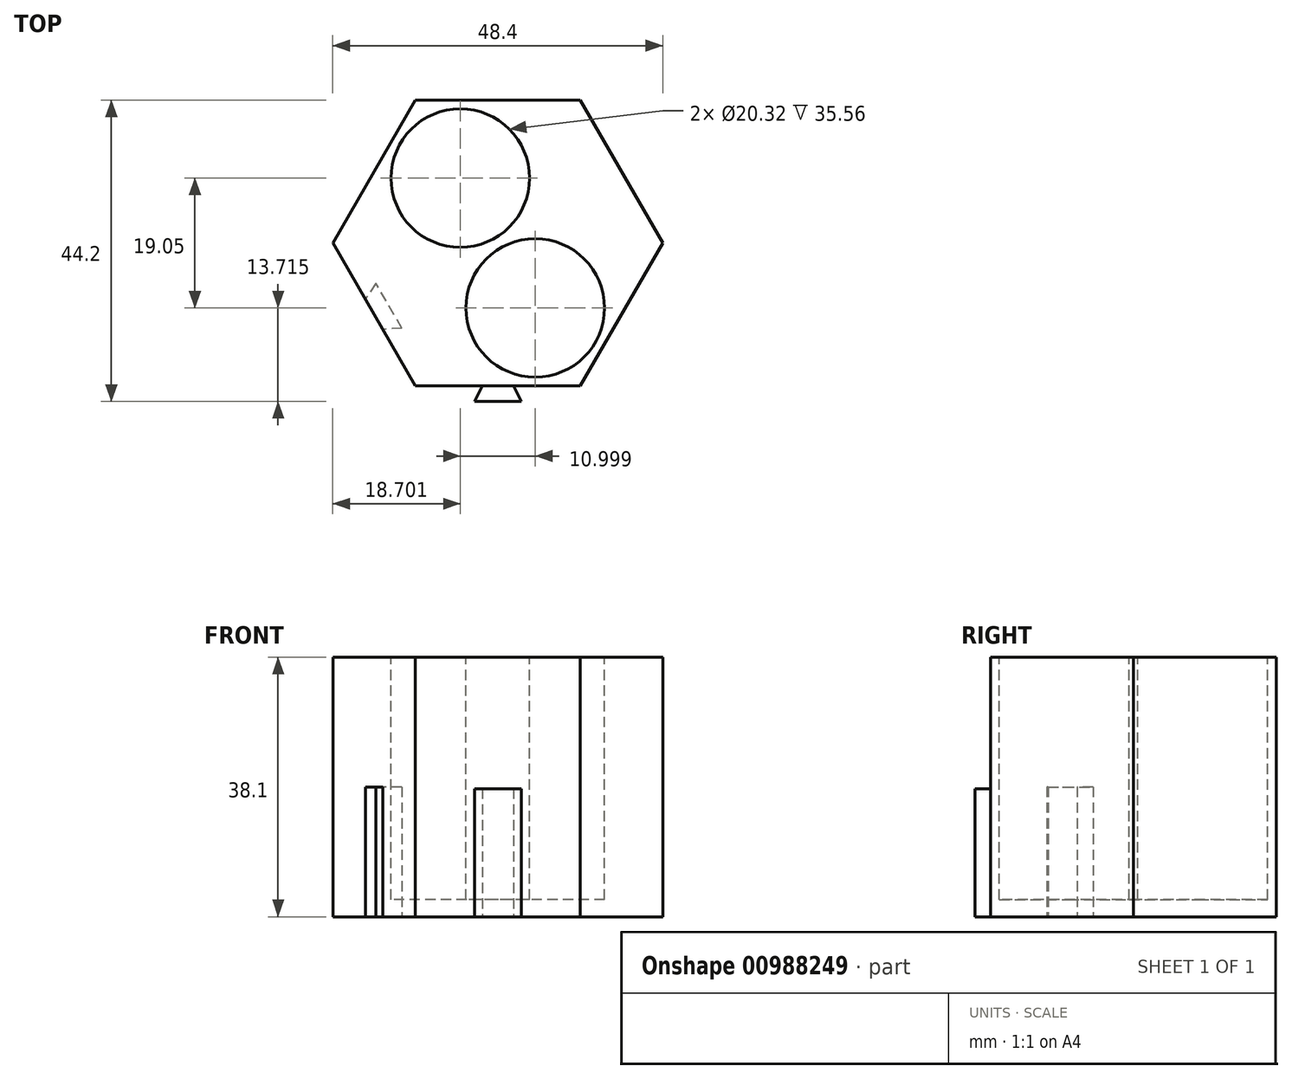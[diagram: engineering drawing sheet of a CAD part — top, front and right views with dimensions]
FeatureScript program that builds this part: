
annotation { "Feature Type Name" : "Feature", "Feature Type Description" : "" }
export const myFeature = defineFeature(function(context is Context, id is Id, definition is map)
    precondition{}
    {
        {
            var Q0;
            Q0=qCreatedBy(makeId("Top.planeOp"),FACE);
            var sketch = newSketch(context, id + "F0", { "sketchPlane" : qUnion([Q0])});
            skCircle(sketch, "E0.cCircle", {"center": v(0, 0) * mm, "radius": 20.96 * mm, "construction": true});
            skLineSegment(sketch, "E0.0", {"start": v(12.1, -20.96) * mm, "end": v(-12.1, -20.96) * mm});
            skLineSegment(sketch, "E0.1", {"start": v(-12.1, -20.96) * mm, "end": v(-24.2, 0) * mm});
            skLineSegment(sketch, "E0.2", {"start": v(-24.2, 0) * mm, "end": v(-12.1, 20.95) * mm});
            skLineSegment(sketch, "E0.3", {"start": v(-12.1, 20.95) * mm, "end": v(12.1, 20.96) * mm});
            skLineSegment(sketch, "E0.4", {"start": v(12.1, 20.96) * mm, "end": v(24.2, 0) * mm});
            skLineSegment(sketch, "E0.5", {"start": v(24.2, 0) * mm, "end": v(12.1, -20.96) * mm});
            skPoint(sketch, "E0.0.midPoint", {"position": v(0, -20.96) * mm});
            skSolve(sketch);
        }
        {
            var Q0;
            Q0 = qSketchRegion(id + "F0", true);
            extrude(context, id + "F1", {"entities" : qUnion([Q0]), "depth" : 38.1 * mm, "offsetDistance" : 25.4 * mm});
        }
        {
            var Q0;
            Q0=makeQuery(id+"F1.opExtrude","CAP_FACE",FACE,{"disambiguationData":[OSD([sQuery(id+"F0.wireOp",EDGE,"E0.0"),sQuery(id+"F0.wireOp",EDGE,"E0.1"),sQuery(id+"F0.wireOp",EDGE,"E0.2"),sQuery(id+"F0.wireOp",EDGE,"E0.3"),sQuery(id+"F0.wireOp",EDGE,"E0.4"),sQuery(id+"F0.wireOp",EDGE,"E0.5")])],"isStart":false});
            var sketch = newSketch(context, id + "F2", { "sketchPlane" : qUnion([Q0])});
            skCircle(sketch, "E1", {"center": v(5.5, -9.53) * mm, "radius": 10.16 * mm});
            skCircle(sketch, "E2", {"center": v(-5.5, 9.52) * mm, "radius": 10.16 * mm});
            skSolve(sketch);
        }
        {
            var Q0;
            Q0=makeQuery(id+"F2.imprint","IMPRINT",FACE,{"disambiguationData":[TD([[makeQuery(id+"F2.imprint","IMPRINT",EDGE,{"derivedFrom":sQuery(id+"F2.wireOp",EDGE,"E2")}),1.0]])]});
            var Q1;
            Q1=makeQuery(id+"F2.imprint","IMPRINT",FACE,{"disambiguationData":[TD([[makeQuery(id+"F2.imprint","IMPRINT",EDGE,{"derivedFrom":sQuery(id+"F2.wireOp",EDGE,"E1")}),1.0]])]});
            extrude(context, id + "F3", {"entities" : qUnion([Q0, Q1]), "operationType" : NewBodyOperationType.REMOVE, "oppositeDirection" : true, "depth" : 35.56 * mm, "offsetDistance" : 25.4 * mm});
        }
        {
            var Q0;
            Q0=makeQuery(id+"F1.opExtrude","CAP_FACE",FACE,{"disambiguationData":[OSD([sQuery(id+"F0.wireOp",EDGE,"E0.0"),sQuery(id+"F0.wireOp",EDGE,"E0.1"),sQuery(id+"F0.wireOp",EDGE,"E0.2"),sQuery(id+"F0.wireOp",EDGE,"E0.3"),sQuery(id+"F0.wireOp",EDGE,"E0.4"),sQuery(id+"F0.wireOp",EDGE,"E0.5")])],"isStart":true});
            var sketch = newSketch(context, id + "F4", { "sketchPlane" : qUnion([Q0])});
            skLineSegment(sketch, "E3", {"start": v(-18.15, 10.48) * mm, "end": v(18.15, -10.48) * mm});
            skLineSegment(sketch, "E4", {"start": v(-18.15, 10.48) * mm, "end": v(-15.95, 9.2) * mm});
            skLineSegment(sketch, "E5", {"start": v(-18.15, 10.48) * mm, "end": v(-19.42, 8.28) * mm});
            skLineSegment(sketch, "E6", {"start": v(-15.95, 9.2) * mm, "end": v(-17.85, 5.9) * mm});
            skLineSegment(sketch, "E7", {"start": v(-17.85, 5.9) * mm, "end": v(-19.42, 8.28) * mm});
            skLineSegment(sketch, "E8.MirrorCS", {"start": v(-15.95, 9.2) * mm, "end": v(-14.04, 12.5) * mm});
            skLineSegment(sketch, "E9.MirrorCS", {"start": v(-14.04, 12.5) * mm, "end": v(-16.88, 12.68) * mm});
            skLineSegment(sketch, "E10.MirrorCS", {"start": v(-18.15, 10.48) * mm, "end": v(-16.88, 12.68) * mm});
            skSolve(sketch);
        }
        {
            var Q0;
            {var subQ0=sQuery(id+"F4.wireOp",EDGE,"E8.MirrorCS");var subQ4=sQuery(id+"F4.wireOp",EDGE,"E5");Q0=qUnion([makeQuery(id+"F4.imprint","IMPRINT",FACE,{"disambiguationData":[TD([[makeQuery(id+"F4.imprint","IMPRINT",EDGE,{"derivedFrom":subQ4}),1.0]])]}),makeQuery(id+"F4.imprint","IMPRINT",FACE,{"disambiguationData":[TD([[makeQuery(id+"F4.imprint","IMPRINT",EDGE,{"derivedFrom":subQ0}),1.0]])]})]);}
            extrude(context, id + "F5", {"entities" : qUnion([Q0]), "operationType" : NewBodyOperationType.REMOVE, "oppositeDirection" : true, "depth" : 19.05 * mm, "offsetDistance" : 25.4 * mm});
        }
        {
            var Q0;
            Q0=makeQuery(id+"F1.opExtrude","CAP_FACE",FACE,{"disambiguationData":[OSD([sQuery(id+"F0.wireOp",EDGE,"E0.0"),sQuery(id+"F0.wireOp",EDGE,"E0.1"),sQuery(id+"F0.wireOp",EDGE,"E0.2"),sQuery(id+"F0.wireOp",EDGE,"E0.3"),sQuery(id+"F0.wireOp",EDGE,"E0.4"),sQuery(id+"F0.wireOp",EDGE,"E0.5")])],"isStart":true});
            var sketch = newSketch(context, id + "F6", { "sketchPlane" : qUnion([Q0])});
            skLineSegment(sketch, "E11", {"start": v(0, 20.96) * mm, "end": v(0, 23.24) * mm});
            skLineSegment(sketch, "E12", {"start": v(0, 20.96) * mm, "end": v(-2.29, 20.96) * mm});
            skLineSegment(sketch, "E13", {"start": v(0, 23.24) * mm, "end": v(-3.43, 23.24) * mm});
            skLineSegment(sketch, "E14", {"start": v(-3.43, 23.24) * mm, "end": v(-2.29, 20.96) * mm});
            skLineSegment(sketch, "E15.MirrorCS", {"start": v(0, 23.24) * mm, "end": v(3.43, 23.24) * mm});
            skLineSegment(sketch, "E16.MirrorCS", {"start": v(3.43, 23.24) * mm, "end": v(2.29, 20.96) * mm});
            skLineSegment(sketch, "E17.MirrorCS", {"start": v(0, 20.96) * mm, "end": v(2.29, 20.96) * mm});
            skSolve(sketch);
        }
        {
            var Q0;
            Q0 = qSketchRegion(id + "F6", true);
            extrude(context, id + "F7", {"entities" : qUnion([Q0]), "operationType" : NewBodyOperationType.ADD, "oppositeDirection" : true, "depth" : 18.8 * mm, "offsetDistance" : 25.4 * mm});
        }
    });
